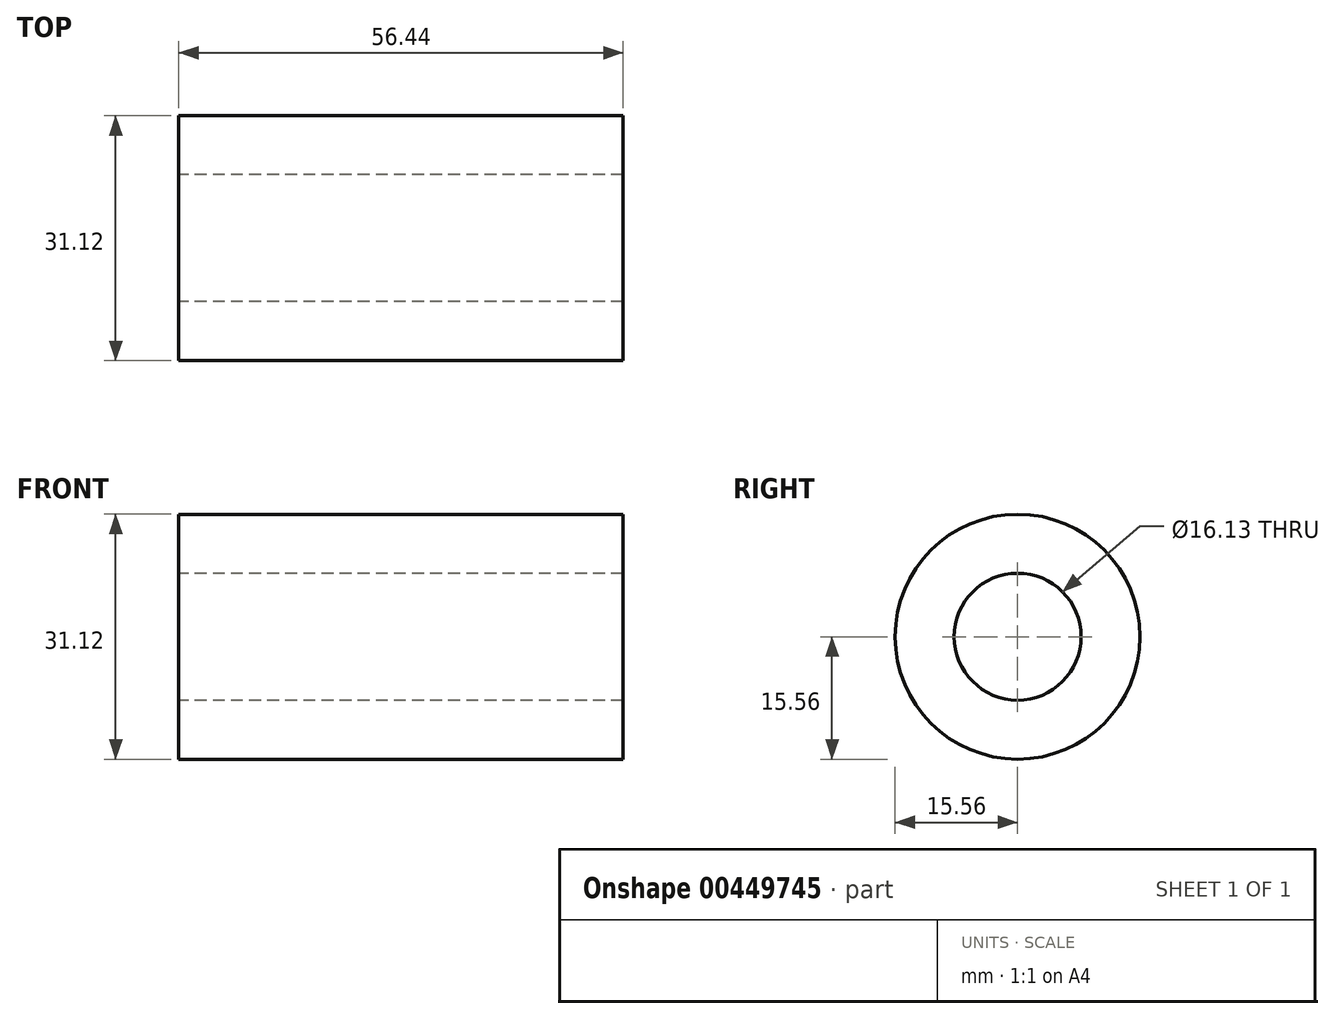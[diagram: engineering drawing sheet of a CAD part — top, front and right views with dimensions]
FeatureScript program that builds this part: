
annotation { "Feature Type Name" : "Feature", "Feature Type Description" : "" }
export const myFeature = defineFeature(function(context is Context, id is Id, definition is map)
    precondition{}
    {
        {
            var Q0;
            Q0=qCreatedBy(makeId("Right.planeOp"),FACE);
            var sketch = newSketch(context, id + "F0", { "sketchPlane" : qUnion([Q0])});
            skCircle(sketch, "E0", {"center": v(0, 0) * mm, "radius": 15.56 * mm});
            skCircle(sketch, "E1", {"center": v(0, 0) * mm, "radius": 8.06 * mm});
            skSolve(sketch);
        }
        {
            var Q0;
            Q0=makeQuery(id+"F0.imprint","IMPRINT",FACE,{"disambiguationData":[TD([[makeQuery(id+"F0.imprint","IMPRINT",EDGE,{"derivedFrom":sQuery(id+"F0.wireOp",EDGE,"E0")}),1.0]])]});
            var Q1;
            Q1=sQuery(id+"F0.wireOp",EDGE,"E0");
            extrude(context, id + "F1", {"entities" : qUnion([Q0]), "surfaceEntities" : qUnion([Q1]), "depth" : 56.44 * mm});
        }
    });
